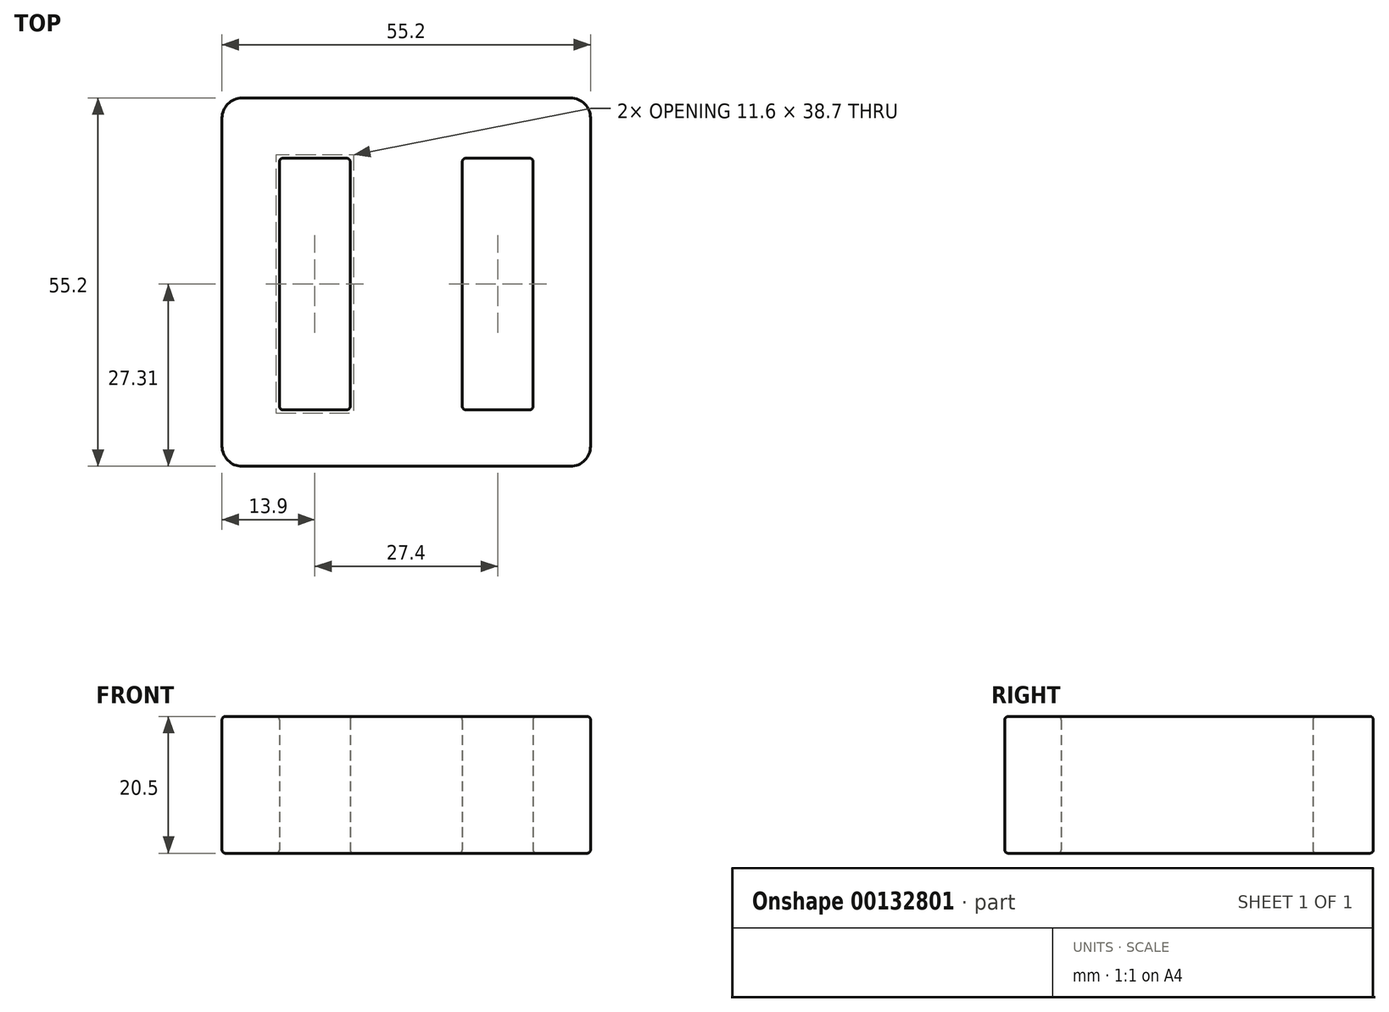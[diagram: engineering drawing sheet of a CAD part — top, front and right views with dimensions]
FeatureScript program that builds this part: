
annotation { "Feature Type Name" : "Feature", "Feature Type Description" : "" }
export const myFeature = defineFeature(function(context is Context, id is Id, definition is map)
    precondition{}
    {
        {
            var Q0;
            Q0=qCreatedBy(makeId("Top.planeOp"),FACE);
            var sketch = newSketch(context, id + "F0", { "sketchPlane" : qUnion([Q0])});
            skLineSegment(sketch, "E0.bottom", {"start": v(27.6, 27.6) * mm, "end": v(-27.6, 27.6) * mm});
            skLineSegment(sketch, "E0.top", {"start": v(27.6, -27.6) * mm, "end": v(-27.6, -27.6) * mm});
            skLineSegment(sketch, "E0.left", {"start": v(27.6, 27.6) * mm, "end": v(27.6, -27.6) * mm});
            skLineSegment(sketch, "E0.right", {"start": v(-27.6, 27.6) * mm, "end": v(-27.6, -27.6) * mm});
            skPoint(sketch, "E0.middle", {"position": v(0, 0) * mm});
            skLineSegment(sketch, "E1.bottom", {"start": v(-19, -19.14) * mm, "end": v(-8.4, -19.14) * mm});
            skLineSegment(sketch, "E1.top", {"start": v(-19, 18.56) * mm, "end": v(-8.4, 18.56) * mm});
            skLineSegment(sketch, "E1.left", {"start": v(-19, -19.14) * mm, "end": v(-19, 18.56) * mm});
            skLineSegment(sketch, "E1.right", {"start": v(-8.4, -19.14) * mm, "end": v(-8.4, 18.56) * mm});
            skLineSegment(sketch, "E2.MirrorCS", {"start": v(19, 18.56) * mm, "end": v(8.4, 18.56) * mm});
            skLineSegment(sketch, "E3.MirrorCS", {"start": v(8.4, -19.14) * mm, "end": v(8.4, 18.56) * mm});
            skLineSegment(sketch, "E4.MirrorCS", {"start": v(19, -19.14) * mm, "end": v(8.4, -19.14) * mm});
            skLineSegment(sketch, "E5.MirrorCS", {"start": v(19, -19.14) * mm, "end": v(19, 18.56) * mm});
            skSolve(sketch);
        }
        {
            var Q0;
            Q0=makeQuery(id+"F0.imprint","IMPRINT",FACE,{"disambiguationData":[TD([[makeQuery(id+"F0.imprint","IMPRINT",EDGE,{"derivedFrom":sQuery(id+"F0.wireOp",EDGE,"E0.bottom")}),1.0]])]});
            extrude(context, id + "F1", {"entities" : qUnion([Q0]), "depth" : 33.5 * mm, "hasSecondDirection" : true, "secondDirectionOppositeDirection" : false, "secondDirectionDepth" : 13 * mm});
        }
        {
            var Q0;
            Q0=makeQuery(id+"F1.opExtrude","SWEPT_EDGE",EDGE,{"disambiguationData":[OSD([sQuery(id+"F0.wireOp",EDGE,"E0.top"),sQuery(id+"F0.wireOp",EDGE,"E0.right")])]});
            var Q1;
            Q1=makeQuery(id+"F1.opExtrude","SWEPT_EDGE",EDGE,{"disambiguationData":[OSD([sQuery(id+"F0.wireOp",EDGE,"E0.top"),sQuery(id+"F0.wireOp",EDGE,"E0.left")])]});
            var Q2;
            Q2=makeQuery(id+"F1.opExtrude","SWEPT_EDGE",EDGE,{"disambiguationData":[OSD([sQuery(id+"F0.wireOp",EDGE,"E0.bottom"),sQuery(id+"F0.wireOp",EDGE,"E0.left")])]});
            var Q3;
            Q3=makeQuery(id+"F1.opExtrude","SWEPT_EDGE",EDGE,{"disambiguationData":[OSD([sQuery(id+"F0.wireOp",EDGE,"E0.bottom"),sQuery(id+"F0.wireOp",EDGE,"E0.right")])]});
            fillet(context, id + "F2", {"entities" : qUnion([Q0, Q1, Q2, Q3]), "radius" : 3 * mm, "tangentPropagation" : true, "allowEdgeOverflow" : false});
        }
        {
            var Q0;
            Q0=makeQuery(id+"F1.opExtrude","CAP_EDGE",EDGE,{"disambiguationData":[OSD([sQuery(id+"F0.wireOp",EDGE,"E1.right")])],"isStart":false});
            var Q1;
            Q1=makeQuery(id+"F1.opExtrude","CAP_EDGE",EDGE,{"disambiguationData":[OSD([sQuery(id+"F0.wireOp",EDGE,"E1.left")])],"isStart":false});
            var Q2;
            Q2=makeQuery(id+"F1.opExtrude","CAP_EDGE",EDGE,{"disambiguationData":[OSD([sQuery(id+"F0.wireOp",EDGE,"E1.top")])],"isStart":false});
            var Q3;
            Q3=makeQuery(id+"F1.opExtrude","CAP_EDGE",EDGE,{"disambiguationData":[OSD([sQuery(id+"F0.wireOp",EDGE,"E3.MirrorCS")])],"isStart":false});
            var Q4;
            Q4=makeQuery(id+"F1.opExtrude","SWEPT_EDGE",EDGE,{"disambiguationData":[OSD([sQuery(id+"F0.wireOp",EDGE,"E1.top"),sQuery(id+"F0.wireOp",EDGE,"E1.left")])]});
            var Q5;
            Q5=makeQuery(id+"F1.opExtrude","CAP_EDGE",EDGE,{"disambiguationData":[OSD([sQuery(id+"F0.wireOp",EDGE,"E1.bottom")])],"isStart":false});
            var Q6;
            Q6=makeQuery(id+"F1.opExtrude","SWEPT_EDGE",EDGE,{"disambiguationData":[OSD([sQuery(id+"F0.wireOp",EDGE,"E2.MirrorCS"),sQuery(id+"F0.wireOp",EDGE,"E3.MirrorCS")])]});
            var Q7;
            Q7=makeQuery(id+"F1.opExtrude","CAP_EDGE",EDGE,{"disambiguationData":[OSD([sQuery(id+"F0.wireOp",EDGE,"E5.MirrorCS")])],"isStart":false});
            var Q8;
            Q8=makeQuery(id+"F1.opExtrude","CAP_EDGE",EDGE,{"disambiguationData":[OSD([sQuery(id+"F0.wireOp",EDGE,"E4.MirrorCS")])],"isStart":false});
            var Q9;
            Q9=makeQuery(id+"F1.opExtrude","CAP_EDGE",EDGE,{"disambiguationData":[OSD([sQuery(id+"F0.wireOp",EDGE,"E0.left")])],"isStart":true});
            var Q10;
            Q10=makeQuery(id+"F1.opExtrude","CAP_EDGE",EDGE,{"disambiguationData":[OSD([sQuery(id+"F0.wireOp",EDGE,"E0.top")])],"isStart":true});
            var Q11;
            Q11=makeQuery(id+"F1.opExtrude","CAP_EDGE",EDGE,{"disambiguationData":[OSD([sQuery(id+"F0.wireOp",EDGE,"E0.left")])],"isStart":false});
            var Q12;
            Q12=makeQuery(id+"F1.opExtrude","CAP_EDGE",EDGE,{"disambiguationData":[OSD([sQuery(id+"F0.wireOp",EDGE,"E0.top")])],"isStart":false});
            var Q13;
            Q13=makeQuery(id+"F1.opExtrude","CAP_EDGE",EDGE,{"disambiguationData":[OSD([sQuery(id+"F0.wireOp",EDGE,"E0.bottom")])],"isStart":false});
            var Q14;
            Q14=makeQuery(id+"F1.opExtrude","CAP_EDGE",EDGE,{"disambiguationData":[OSD([sQuery(id+"F0.wireOp",EDGE,"E1.top")])],"isStart":true});
            var Q15;
            Q15=makeQuery(id+"F1.opExtrude","CAP_EDGE",EDGE,{"disambiguationData":[OSD([sQuery(id+"F0.wireOp",EDGE,"E2.MirrorCS")])],"isStart":false});
            var Q16;
            Q16=makeQuery(id+"F1.opExtrude","CAP_EDGE",EDGE,{"disambiguationData":[OSD([sQuery(id+"F0.wireOp",EDGE,"E1.bottom")])],"isStart":true});
            var Q17;
            Q17=makeQuery(id+"F1.opExtrude","CAP_EDGE",EDGE,{"disambiguationData":[OSD([sQuery(id+"F0.wireOp",EDGE,"E5.MirrorCS")])],"isStart":true});
            var Q18;
            {var subQ0=sQuery(id+"F0.wireOp",EDGE,"E0.top");Q18=makeQuery(id+"F2.opFillet","BLEND_EDGE",EDGE,{"blendedFrom":[makeQuery(id+"F1.opExtrude","SWEPT_EDGE",EDGE,{"disambiguationData":[OSD([subQ0,sQuery(id+"F0.wireOp",EDGE,"E0.right")])]}),makeQuery(id+"F1.opExtrude","SWEPT_FACE",FACE,{"disambiguationData":[OSD([subQ0])]})],"blendedInto":[makeQuery(id+"F1.opExtrude","SWEPT_FACE",FACE,{"disambiguationData":[OSD([subQ0])]})]});}
            var Q19;
            Q19=makeQuery(id+"F1.opExtrude","CAP_EDGE",EDGE,{"disambiguationData":[OSD([sQuery(id+"F0.wireOp",EDGE,"E2.MirrorCS")])],"isStart":true});
            var Q20;
            {var subQ0=sQuery(id+"F0.wireOp",EDGE,"E0.right");var subQ1=sQuery(id+"F0.wireOp",EDGE,"E0.top");Q20=makeQuery(id+"F2.opFillet","BLEND_EDGE",EDGE,{"blendedFrom":[makeQuery(id+"F1.opExtrude","SWEPT_EDGE",EDGE,{"disambiguationData":[OSD([subQ1,subQ0])]}),makeQuery(id+"F1.opExtrude","CAP_FACE",FACE,{"disambiguationData":[OSD([sQuery(id+"F0.wireOp",EDGE,"E0.bottom"),subQ1,sQuery(id+"F0.wireOp",EDGE,"E0.left"),subQ0,sQuery(id+"F0.wireOp",EDGE,"E1.bottom"),sQuery(id+"F0.wireOp",EDGE,"E1.top"),sQuery(id+"F0.wireOp",EDGE,"E1.left"),sQuery(id+"F0.wireOp",EDGE,"E1.right"),sQuery(id+"F0.wireOp",EDGE,"E2.MirrorCS"),sQuery(id+"F0.wireOp",EDGE,"E3.MirrorCS"),sQuery(id+"F0.wireOp",EDGE,"E4.MirrorCS"),sQuery(id+"F0.wireOp",EDGE,"E5.MirrorCS")])],"isStart":false})],"blendedInto":[makeQuery(id+"F1.opExtrude","CAP_FACE",FACE,{"disambiguationData":[OSD([sQuery(id+"F0.wireOp",EDGE,"E0.bottom"),subQ1,sQuery(id+"F0.wireOp",EDGE,"E0.left"),subQ0,sQuery(id+"F0.wireOp",EDGE,"E1.bottom"),sQuery(id+"F0.wireOp",EDGE,"E1.top"),sQuery(id+"F0.wireOp",EDGE,"E1.left"),sQuery(id+"F0.wireOp",EDGE,"E1.right"),sQuery(id+"F0.wireOp",EDGE,"E2.MirrorCS"),sQuery(id+"F0.wireOp",EDGE,"E3.MirrorCS"),sQuery(id+"F0.wireOp",EDGE,"E4.MirrorCS"),sQuery(id+"F0.wireOp",EDGE,"E5.MirrorCS")])],"isStart":false})]});}
            var Q21;
            {var subQ0=sQuery(id+"F0.wireOp",EDGE,"E0.right");Q21=makeQuery(id+"F2.opFillet","BLEND_EDGE",EDGE,{"blendedFrom":[makeQuery(id+"F1.opExtrude","SWEPT_EDGE",EDGE,{"disambiguationData":[OSD([sQuery(id+"F0.wireOp",EDGE,"E0.top"),subQ0])]}),makeQuery(id+"F1.opExtrude","SWEPT_FACE",FACE,{"disambiguationData":[OSD([subQ0])]})],"blendedInto":[makeQuery(id+"F1.opExtrude","SWEPT_FACE",FACE,{"disambiguationData":[OSD([subQ0])]})]});}
            var Q22;
            {var subQ0=sQuery(id+"F0.wireOp",EDGE,"E0.bottom");Q22=makeQuery(id+"F2.opFillet","BLEND_EDGE",EDGE,{"blendedFrom":[makeQuery(id+"F1.opExtrude","SWEPT_EDGE",EDGE,{"disambiguationData":[OSD([subQ0,sQuery(id+"F0.wireOp",EDGE,"E0.left")])]}),makeQuery(id+"F1.opExtrude","SWEPT_FACE",FACE,{"disambiguationData":[OSD([subQ0])]})],"blendedInto":[makeQuery(id+"F1.opExtrude","SWEPT_FACE",FACE,{"disambiguationData":[OSD([subQ0])]})]});}
            var Q23;
            {var subQ0=sQuery(id+"F0.wireOp",EDGE,"E0.left");var subQ1=sQuery(id+"F0.wireOp",EDGE,"E0.bottom");Q23=makeQuery(id+"F2.opFillet","BLEND_EDGE",EDGE,{"blendedFrom":[makeQuery(id+"F1.opExtrude","SWEPT_EDGE",EDGE,{"disambiguationData":[OSD([subQ1,subQ0])]}),makeQuery(id+"F1.opExtrude","CAP_FACE",FACE,{"disambiguationData":[OSD([subQ1,sQuery(id+"F0.wireOp",EDGE,"E0.top"),subQ0,sQuery(id+"F0.wireOp",EDGE,"E0.right"),sQuery(id+"F0.wireOp",EDGE,"E1.bottom"),sQuery(id+"F0.wireOp",EDGE,"E1.top"),sQuery(id+"F0.wireOp",EDGE,"E1.left"),sQuery(id+"F0.wireOp",EDGE,"E1.right"),sQuery(id+"F0.wireOp",EDGE,"E2.MirrorCS"),sQuery(id+"F0.wireOp",EDGE,"E3.MirrorCS"),sQuery(id+"F0.wireOp",EDGE,"E4.MirrorCS"),sQuery(id+"F0.wireOp",EDGE,"E5.MirrorCS")])],"isStart":true})],"blendedInto":[makeQuery(id+"F1.opExtrude","CAP_FACE",FACE,{"disambiguationData":[OSD([subQ1,sQuery(id+"F0.wireOp",EDGE,"E0.top"),subQ0,sQuery(id+"F0.wireOp",EDGE,"E0.right"),sQuery(id+"F0.wireOp",EDGE,"E1.bottom"),sQuery(id+"F0.wireOp",EDGE,"E1.top"),sQuery(id+"F0.wireOp",EDGE,"E1.left"),sQuery(id+"F0.wireOp",EDGE,"E1.right"),sQuery(id+"F0.wireOp",EDGE,"E2.MirrorCS"),sQuery(id+"F0.wireOp",EDGE,"E3.MirrorCS"),sQuery(id+"F0.wireOp",EDGE,"E4.MirrorCS"),sQuery(id+"F0.wireOp",EDGE,"E5.MirrorCS")])],"isStart":true})]});}
            var Q24;
            Q24=makeQuery(id+"F1.opExtrude","CAP_EDGE",EDGE,{"disambiguationData":[OSD([sQuery(id+"F0.wireOp",EDGE,"E1.right")])],"isStart":true});
            var Q25;
            {var subQ0=sQuery(id+"F0.wireOp",EDGE,"E0.left");var subQ1=sQuery(id+"F0.wireOp",EDGE,"E0.bottom");Q25=makeQuery(id+"F2.opFillet","BLEND_EDGE",EDGE,{"blendedFrom":[makeQuery(id+"F1.opExtrude","SWEPT_EDGE",EDGE,{"disambiguationData":[OSD([subQ1,subQ0])]}),makeQuery(id+"F1.opExtrude","CAP_FACE",FACE,{"disambiguationData":[OSD([subQ1,sQuery(id+"F0.wireOp",EDGE,"E0.top"),subQ0,sQuery(id+"F0.wireOp",EDGE,"E0.right"),sQuery(id+"F0.wireOp",EDGE,"E1.bottom"),sQuery(id+"F0.wireOp",EDGE,"E1.top"),sQuery(id+"F0.wireOp",EDGE,"E1.left"),sQuery(id+"F0.wireOp",EDGE,"E1.right"),sQuery(id+"F0.wireOp",EDGE,"E2.MirrorCS"),sQuery(id+"F0.wireOp",EDGE,"E3.MirrorCS"),sQuery(id+"F0.wireOp",EDGE,"E4.MirrorCS"),sQuery(id+"F0.wireOp",EDGE,"E5.MirrorCS")])],"isStart":false})],"blendedInto":[makeQuery(id+"F1.opExtrude","CAP_FACE",FACE,{"disambiguationData":[OSD([subQ1,sQuery(id+"F0.wireOp",EDGE,"E0.top"),subQ0,sQuery(id+"F0.wireOp",EDGE,"E0.right"),sQuery(id+"F0.wireOp",EDGE,"E1.bottom"),sQuery(id+"F0.wireOp",EDGE,"E1.top"),sQuery(id+"F0.wireOp",EDGE,"E1.left"),sQuery(id+"F0.wireOp",EDGE,"E1.right"),sQuery(id+"F0.wireOp",EDGE,"E2.MirrorCS"),sQuery(id+"F0.wireOp",EDGE,"E3.MirrorCS"),sQuery(id+"F0.wireOp",EDGE,"E4.MirrorCS"),sQuery(id+"F0.wireOp",EDGE,"E5.MirrorCS")])],"isStart":false})]});}
            var Q26;
            {var subQ0=sQuery(id+"F0.wireOp",EDGE,"E0.left");Q26=makeQuery(id+"F2.opFillet","BLEND_EDGE",EDGE,{"blendedFrom":[makeQuery(id+"F1.opExtrude","SWEPT_EDGE",EDGE,{"disambiguationData":[OSD([sQuery(id+"F0.wireOp",EDGE,"E0.bottom"),subQ0])]}),makeQuery(id+"F1.opExtrude","SWEPT_FACE",FACE,{"disambiguationData":[OSD([subQ0])]})],"blendedInto":[makeQuery(id+"F1.opExtrude","SWEPT_FACE",FACE,{"disambiguationData":[OSD([subQ0])]})]});}
            var Q27;
            Q27=makeQuery(id+"F1.opExtrude","CAP_EDGE",EDGE,{"disambiguationData":[OSD([sQuery(id+"F0.wireOp",EDGE,"E1.left")])],"isStart":true});
            var Q28;
            Q28=makeQuery(id+"F1.opExtrude","SWEPT_EDGE",EDGE,{"disambiguationData":[OSD([sQuery(id+"F0.wireOp",EDGE,"E1.bottom"),sQuery(id+"F0.wireOp",EDGE,"E1.left")])]});
            var Q29;
            Q29=makeQuery(id+"F1.opExtrude","SWEPT_EDGE",EDGE,{"disambiguationData":[OSD([sQuery(id+"F0.wireOp",EDGE,"E1.bottom"),sQuery(id+"F0.wireOp",EDGE,"E1.right")])]});
            var Q30;
            Q30=makeQuery(id+"F1.opExtrude","SWEPT_EDGE",EDGE,{"disambiguationData":[OSD([sQuery(id+"F0.wireOp",EDGE,"E1.top"),sQuery(id+"F0.wireOp",EDGE,"E1.right")])]});
            var Q31;
            Q31=makeQuery(id+"F1.opExtrude","CAP_EDGE",EDGE,{"disambiguationData":[OSD([sQuery(id+"F0.wireOp",EDGE,"E3.MirrorCS")])],"isStart":true});
            var Q32;
            Q32=makeQuery(id+"F1.opExtrude","SWEPT_EDGE",EDGE,{"disambiguationData":[OSD([sQuery(id+"F0.wireOp",EDGE,"E2.MirrorCS"),sQuery(id+"F0.wireOp",EDGE,"E5.MirrorCS")])]});
            var Q33;
            Q33=makeQuery(id+"F1.opExtrude","SWEPT_EDGE",EDGE,{"disambiguationData":[OSD([sQuery(id+"F0.wireOp",EDGE,"E3.MirrorCS"),sQuery(id+"F0.wireOp",EDGE,"E4.MirrorCS")])]});
            var Q34;
            Q34=makeQuery(id+"F1.opExtrude","SWEPT_EDGE",EDGE,{"disambiguationData":[OSD([sQuery(id+"F0.wireOp",EDGE,"E4.MirrorCS"),sQuery(id+"F0.wireOp",EDGE,"E5.MirrorCS")])]});
            var Q35;
            {var subQ0=sQuery(id+"F0.wireOp",EDGE,"E0.left");var subQ1=sQuery(id+"F0.wireOp",EDGE,"E0.top");Q35=makeQuery(id+"F2.opFillet","BLEND_EDGE",EDGE,{"blendedFrom":[makeQuery(id+"F1.opExtrude","SWEPT_EDGE",EDGE,{"disambiguationData":[OSD([subQ1,subQ0])]}),makeQuery(id+"F1.opExtrude","CAP_FACE",FACE,{"disambiguationData":[OSD([sQuery(id+"F0.wireOp",EDGE,"E0.bottom"),subQ1,subQ0,sQuery(id+"F0.wireOp",EDGE,"E0.right"),sQuery(id+"F0.wireOp",EDGE,"E1.bottom"),sQuery(id+"F0.wireOp",EDGE,"E1.top"),sQuery(id+"F0.wireOp",EDGE,"E1.left"),sQuery(id+"F0.wireOp",EDGE,"E1.right"),sQuery(id+"F0.wireOp",EDGE,"E2.MirrorCS"),sQuery(id+"F0.wireOp",EDGE,"E3.MirrorCS"),sQuery(id+"F0.wireOp",EDGE,"E4.MirrorCS"),sQuery(id+"F0.wireOp",EDGE,"E5.MirrorCS")])],"isStart":true})],"blendedInto":[makeQuery(id+"F1.opExtrude","CAP_FACE",FACE,{"disambiguationData":[OSD([sQuery(id+"F0.wireOp",EDGE,"E0.bottom"),subQ1,subQ0,sQuery(id+"F0.wireOp",EDGE,"E0.right"),sQuery(id+"F0.wireOp",EDGE,"E1.bottom"),sQuery(id+"F0.wireOp",EDGE,"E1.top"),sQuery(id+"F0.wireOp",EDGE,"E1.left"),sQuery(id+"F0.wireOp",EDGE,"E1.right"),sQuery(id+"F0.wireOp",EDGE,"E2.MirrorCS"),sQuery(id+"F0.wireOp",EDGE,"E3.MirrorCS"),sQuery(id+"F0.wireOp",EDGE,"E4.MirrorCS"),sQuery(id+"F0.wireOp",EDGE,"E5.MirrorCS")])],"isStart":true})]});}
            var Q36;
            {var subQ0=sQuery(id+"F0.wireOp",EDGE,"E0.left");var subQ1=sQuery(id+"F0.wireOp",EDGE,"E0.top");Q36=makeQuery(id+"F2.opFillet","BLEND_EDGE",EDGE,{"blendedFrom":[makeQuery(id+"F1.opExtrude","SWEPT_EDGE",EDGE,{"disambiguationData":[OSD([subQ1,subQ0])]}),makeQuery(id+"F1.opExtrude","CAP_FACE",FACE,{"disambiguationData":[OSD([sQuery(id+"F0.wireOp",EDGE,"E0.bottom"),subQ1,subQ0,sQuery(id+"F0.wireOp",EDGE,"E0.right"),sQuery(id+"F0.wireOp",EDGE,"E1.bottom"),sQuery(id+"F0.wireOp",EDGE,"E1.top"),sQuery(id+"F0.wireOp",EDGE,"E1.left"),sQuery(id+"F0.wireOp",EDGE,"E1.right"),sQuery(id+"F0.wireOp",EDGE,"E2.MirrorCS"),sQuery(id+"F0.wireOp",EDGE,"E3.MirrorCS"),sQuery(id+"F0.wireOp",EDGE,"E4.MirrorCS"),sQuery(id+"F0.wireOp",EDGE,"E5.MirrorCS")])],"isStart":false})],"blendedInto":[makeQuery(id+"F1.opExtrude","CAP_FACE",FACE,{"disambiguationData":[OSD([sQuery(id+"F0.wireOp",EDGE,"E0.bottom"),subQ1,subQ0,sQuery(id+"F0.wireOp",EDGE,"E0.right"),sQuery(id+"F0.wireOp",EDGE,"E1.bottom"),sQuery(id+"F0.wireOp",EDGE,"E1.top"),sQuery(id+"F0.wireOp",EDGE,"E1.left"),sQuery(id+"F0.wireOp",EDGE,"E1.right"),sQuery(id+"F0.wireOp",EDGE,"E2.MirrorCS"),sQuery(id+"F0.wireOp",EDGE,"E3.MirrorCS"),sQuery(id+"F0.wireOp",EDGE,"E4.MirrorCS"),sQuery(id+"F0.wireOp",EDGE,"E5.MirrorCS")])],"isStart":false})]});}
            var Q37;
            {var subQ0=sQuery(id+"F0.wireOp",EDGE,"E0.top");Q37=makeQuery(id+"F2.opFillet","BLEND_EDGE",EDGE,{"blendedFrom":[makeQuery(id+"F1.opExtrude","SWEPT_EDGE",EDGE,{"disambiguationData":[OSD([subQ0,sQuery(id+"F0.wireOp",EDGE,"E0.left")])]}),makeQuery(id+"F1.opExtrude","SWEPT_FACE",FACE,{"disambiguationData":[OSD([subQ0])]})],"blendedInto":[makeQuery(id+"F1.opExtrude","SWEPT_FACE",FACE,{"disambiguationData":[OSD([subQ0])]})]});}
            var Q38;
            {var subQ0=sQuery(id+"F0.wireOp",EDGE,"E0.left");Q38=makeQuery(id+"F2.opFillet","BLEND_EDGE",EDGE,{"blendedFrom":[makeQuery(id+"F1.opExtrude","SWEPT_EDGE",EDGE,{"disambiguationData":[OSD([sQuery(id+"F0.wireOp",EDGE,"E0.top"),subQ0])]}),makeQuery(id+"F1.opExtrude","SWEPT_FACE",FACE,{"disambiguationData":[OSD([subQ0])]})],"blendedInto":[makeQuery(id+"F1.opExtrude","SWEPT_FACE",FACE,{"disambiguationData":[OSD([subQ0])]})]});}
            var Q39;
            {var subQ0=sQuery(id+"F0.wireOp",EDGE,"E0.right");var subQ1=sQuery(id+"F0.wireOp",EDGE,"E0.top");Q39=makeQuery(id+"F2.opFillet","BLEND_EDGE",EDGE,{"blendedFrom":[makeQuery(id+"F1.opExtrude","SWEPT_EDGE",EDGE,{"disambiguationData":[OSD([subQ1,subQ0])]}),makeQuery(id+"F1.opExtrude","CAP_FACE",FACE,{"disambiguationData":[OSD([sQuery(id+"F0.wireOp",EDGE,"E0.bottom"),subQ1,sQuery(id+"F0.wireOp",EDGE,"E0.left"),subQ0,sQuery(id+"F0.wireOp",EDGE,"E1.bottom"),sQuery(id+"F0.wireOp",EDGE,"E1.top"),sQuery(id+"F0.wireOp",EDGE,"E1.left"),sQuery(id+"F0.wireOp",EDGE,"E1.right"),sQuery(id+"F0.wireOp",EDGE,"E2.MirrorCS"),sQuery(id+"F0.wireOp",EDGE,"E3.MirrorCS"),sQuery(id+"F0.wireOp",EDGE,"E4.MirrorCS"),sQuery(id+"F0.wireOp",EDGE,"E5.MirrorCS")])],"isStart":true})],"blendedInto":[makeQuery(id+"F1.opExtrude","CAP_FACE",FACE,{"disambiguationData":[OSD([sQuery(id+"F0.wireOp",EDGE,"E0.bottom"),subQ1,sQuery(id+"F0.wireOp",EDGE,"E0.left"),subQ0,sQuery(id+"F0.wireOp",EDGE,"E1.bottom"),sQuery(id+"F0.wireOp",EDGE,"E1.top"),sQuery(id+"F0.wireOp",EDGE,"E1.left"),sQuery(id+"F0.wireOp",EDGE,"E1.right"),sQuery(id+"F0.wireOp",EDGE,"E2.MirrorCS"),sQuery(id+"F0.wireOp",EDGE,"E3.MirrorCS"),sQuery(id+"F0.wireOp",EDGE,"E4.MirrorCS"),sQuery(id+"F0.wireOp",EDGE,"E5.MirrorCS")])],"isStart":true})]});}
            var Q40;
            Q40=makeQuery(id+"F1.opExtrude","CAP_EDGE",EDGE,{"disambiguationData":[OSD([sQuery(id+"F0.wireOp",EDGE,"E0.right")])],"isStart":false});
            var Q41;
            Q41=makeQuery(id+"F1.opExtrude","CAP_EDGE",EDGE,{"disambiguationData":[OSD([sQuery(id+"F0.wireOp",EDGE,"E0.right")])],"isStart":true});
            var Q42;
            Q42=makeQuery(id+"F1.opExtrude","CAP_EDGE",EDGE,{"disambiguationData":[OSD([sQuery(id+"F0.wireOp",EDGE,"E0.bottom")])],"isStart":true});
            var Q43;
            {var subQ0=sQuery(id+"F0.wireOp",EDGE,"E0.right");Q43=makeQuery(id+"F2.opFillet","BLEND_EDGE",EDGE,{"blendedFrom":[makeQuery(id+"F1.opExtrude","SWEPT_EDGE",EDGE,{"disambiguationData":[OSD([sQuery(id+"F0.wireOp",EDGE,"E0.bottom"),subQ0])]}),makeQuery(id+"F1.opExtrude","SWEPT_FACE",FACE,{"disambiguationData":[OSD([subQ0])]})],"blendedInto":[makeQuery(id+"F1.opExtrude","SWEPT_FACE",FACE,{"disambiguationData":[OSD([subQ0])]})]});}
            var Q44;
            Q44=makeQuery(id+"F1.opExtrude","CAP_EDGE",EDGE,{"disambiguationData":[OSD([sQuery(id+"F0.wireOp",EDGE,"E4.MirrorCS")])],"isStart":true});
            var Q45;
            {var subQ0=sQuery(id+"F0.wireOp",EDGE,"E0.bottom");Q45=makeQuery(id+"F2.opFillet","BLEND_EDGE",EDGE,{"blendedFrom":[makeQuery(id+"F1.opExtrude","SWEPT_EDGE",EDGE,{"disambiguationData":[OSD([subQ0,sQuery(id+"F0.wireOp",EDGE,"E0.right")])]}),makeQuery(id+"F1.opExtrude","SWEPT_FACE",FACE,{"disambiguationData":[OSD([subQ0])]})],"blendedInto":[makeQuery(id+"F1.opExtrude","SWEPT_FACE",FACE,{"disambiguationData":[OSD([subQ0])]})]});}
            var Q46;
            {var subQ0=sQuery(id+"F0.wireOp",EDGE,"E0.right");var subQ1=sQuery(id+"F0.wireOp",EDGE,"E0.bottom");Q46=makeQuery(id+"F2.opFillet","BLEND_EDGE",EDGE,{"blendedFrom":[makeQuery(id+"F1.opExtrude","SWEPT_EDGE",EDGE,{"disambiguationData":[OSD([subQ1,subQ0])]}),makeQuery(id+"F1.opExtrude","CAP_FACE",FACE,{"disambiguationData":[OSD([subQ1,sQuery(id+"F0.wireOp",EDGE,"E0.top"),sQuery(id+"F0.wireOp",EDGE,"E0.left"),subQ0,sQuery(id+"F0.wireOp",EDGE,"E1.bottom"),sQuery(id+"F0.wireOp",EDGE,"E1.top"),sQuery(id+"F0.wireOp",EDGE,"E1.left"),sQuery(id+"F0.wireOp",EDGE,"E1.right"),sQuery(id+"F0.wireOp",EDGE,"E2.MirrorCS"),sQuery(id+"F0.wireOp",EDGE,"E3.MirrorCS"),sQuery(id+"F0.wireOp",EDGE,"E4.MirrorCS"),sQuery(id+"F0.wireOp",EDGE,"E5.MirrorCS")])],"isStart":true})],"blendedInto":[makeQuery(id+"F1.opExtrude","CAP_FACE",FACE,{"disambiguationData":[OSD([subQ1,sQuery(id+"F0.wireOp",EDGE,"E0.top"),sQuery(id+"F0.wireOp",EDGE,"E0.left"),subQ0,sQuery(id+"F0.wireOp",EDGE,"E1.bottom"),sQuery(id+"F0.wireOp",EDGE,"E1.top"),sQuery(id+"F0.wireOp",EDGE,"E1.left"),sQuery(id+"F0.wireOp",EDGE,"E1.right"),sQuery(id+"F0.wireOp",EDGE,"E2.MirrorCS"),sQuery(id+"F0.wireOp",EDGE,"E3.MirrorCS"),sQuery(id+"F0.wireOp",EDGE,"E4.MirrorCS"),sQuery(id+"F0.wireOp",EDGE,"E5.MirrorCS")])],"isStart":true})]});}
            var Q47;
            {var subQ0=sQuery(id+"F0.wireOp",EDGE,"E0.right");var subQ1=sQuery(id+"F0.wireOp",EDGE,"E0.bottom");Q47=makeQuery(id+"F2.opFillet","BLEND_EDGE",EDGE,{"blendedFrom":[makeQuery(id+"F1.opExtrude","SWEPT_EDGE",EDGE,{"disambiguationData":[OSD([subQ1,subQ0])]}),makeQuery(id+"F1.opExtrude","CAP_FACE",FACE,{"disambiguationData":[OSD([subQ1,sQuery(id+"F0.wireOp",EDGE,"E0.top"),sQuery(id+"F0.wireOp",EDGE,"E0.left"),subQ0,sQuery(id+"F0.wireOp",EDGE,"E1.bottom"),sQuery(id+"F0.wireOp",EDGE,"E1.top"),sQuery(id+"F0.wireOp",EDGE,"E1.left"),sQuery(id+"F0.wireOp",EDGE,"E1.right"),sQuery(id+"F0.wireOp",EDGE,"E2.MirrorCS"),sQuery(id+"F0.wireOp",EDGE,"E3.MirrorCS"),sQuery(id+"F0.wireOp",EDGE,"E4.MirrorCS"),sQuery(id+"F0.wireOp",EDGE,"E5.MirrorCS")])],"isStart":false})],"blendedInto":[makeQuery(id+"F1.opExtrude","CAP_FACE",FACE,{"disambiguationData":[OSD([subQ1,sQuery(id+"F0.wireOp",EDGE,"E0.top"),sQuery(id+"F0.wireOp",EDGE,"E0.left"),subQ0,sQuery(id+"F0.wireOp",EDGE,"E1.bottom"),sQuery(id+"F0.wireOp",EDGE,"E1.top"),sQuery(id+"F0.wireOp",EDGE,"E1.left"),sQuery(id+"F0.wireOp",EDGE,"E1.right"),sQuery(id+"F0.wireOp",EDGE,"E2.MirrorCS"),sQuery(id+"F0.wireOp",EDGE,"E3.MirrorCS"),sQuery(id+"F0.wireOp",EDGE,"E4.MirrorCS"),sQuery(id+"F0.wireOp",EDGE,"E5.MirrorCS")])],"isStart":false})]});}
            fillet(context, id + "F3", {"entities" : qUnion([Q0, Q1, Q2, Q3, Q4, Q5, Q6, Q7, Q8, Q9, Q10, Q11, Q12, Q13, Q14, Q15, Q16, Q17, Q18, Q19, Q20, Q21, Q22, Q23, Q24, Q25, Q26, Q27, Q28, Q29, Q30, Q31, Q32, Q33, Q34, Q35, Q36, Q37, Q38, Q39, Q40, Q41, Q42, Q43, Q44, Q45, Q46, Q47]), "radius" : 0.5 * mm, "tangentPropagation" : true, "allowEdgeOverflow" : false});
        }
    });
